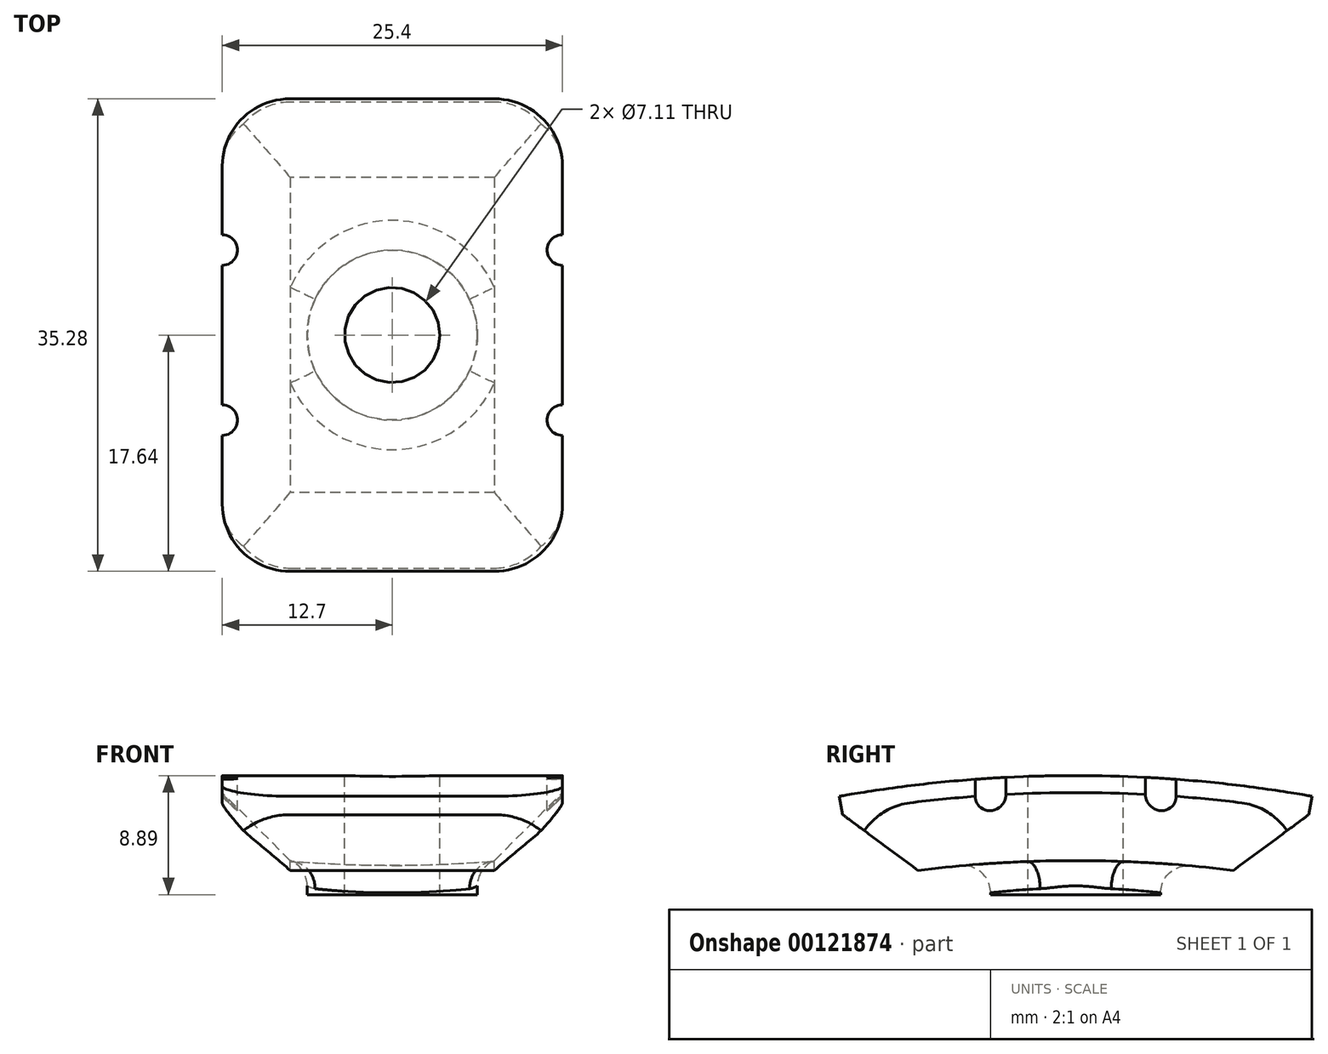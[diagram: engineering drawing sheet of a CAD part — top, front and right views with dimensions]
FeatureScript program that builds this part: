
annotation { "Feature Type Name" : "Feature", "Feature Type Description" : "" }
export const myFeature = defineFeature(function(context is Context, id is Id, definition is map)
    precondition{}
    {
        {
            var Q0;
            Q0=qCreatedBy(makeId("Right.planeOp"),FACE);
            var sketch = newSketch(context, id + "F0", { "sketchPlane" : qUnion([Q0])});
            skArc(sketch, "E0", {"start": v(17.64, -1.54) * mm, "mid": v(0, 0) * mm, "end": v(-17.64, -1.54) * mm});
            skArc(sketch, "E1", {"start": v(16.54, -7.8) * mm, "mid": v(0, -6.35) * mm, "end": v(-16.54, -7.8) * mm});
            skLineSegment(sketch, "E2", {"start": v(-16.54, -7.8) * mm, "end": v(-17.64, -1.54) * mm});
            skLineSegment(sketch, "E3.MirrorCS", {"start": v(16.54, -7.8) * mm, "end": v(17.64, -1.54) * mm});
            skSolve(sketch);
        }
        {
            var Q0;
            Q0=makeQuery(id+"F0.imprint","IMPRINT",FACE,{"disambiguationData":[TD([[makeQuery(id+"F0.imprint","IMPRINT",EDGE,{"derivedFrom":sQuery(id+"F0.wireOp",EDGE,"E0")}),1.0]])]});
            extrude(context, id + "F1", {"entities" : qUnion([Q0]), "endBound" : BoundingType.SYMMETRIC, "depth" : 25.4 * mm});
        }
        {
            var Q0;
            Q0=qCreatedBy(makeId("Top.planeOp"),FACE);
            var sketch = newSketch(context, id + "F2", { "sketchPlane" : qUnion([Q0])});
            skCircle(sketch, "E4", {"center": v(0, 0) * mm, "radius": 3.56 * mm});
            skLineSegment(sketch, "E5.bottom", {"start": v(12.7, 6.35) * mm, "end": v(-12.7, 6.35) * mm});
            skLineSegment(sketch, "E5.top", {"start": v(12.7, -6.35) * mm, "end": v(-12.7, -6.35) * mm});
            skLineSegment(sketch, "E5.left", {"start": v(12.7, 6.35) * mm, "end": v(12.7, -6.35) * mm});
            skLineSegment(sketch, "E5.right", {"start": v(-12.7, 6.35) * mm, "end": v(-12.7, -6.35) * mm});
            skCircle(sketch, "E6", {"center": v(12.7, 6.35) * mm, "radius": 1.14 * mm});
            skCircle(sketch, "E7", {"center": v(-12.7, 6.35) * mm, "radius": 1.14 * mm});
            skCircle(sketch, "E8", {"center": v(12.7, -6.35) * mm, "radius": 1.14 * mm});
            skCircle(sketch, "E9", {"center": v(-12.7, -6.35) * mm, "radius": 1.14 * mm});
            skSolve(sketch);
        }
        {
            var Q0;
            Q0=makeQuery(id+"F2.imprint","IMPRINT",FACE,{"disambiguationData":[TD([[makeQuery(id+"F2.imprint","IMPRINT",EDGE,{"derivedFrom":sQuery(id+"F2.wireOp",EDGE,"E4")}),1.0]])]});
            extrude(context, id + "F3", {"entities" : qUnion([Q0]), "operationType" : NewBodyOperationType.REMOVE, "oppositeDirection" : true, "depth" : 25.4 * mm});
        }
        {
            var Q0;
            {var subQ0=sQuery(id+"F2.wireOp",EDGE,"E5.right");var subQ1=sQuery(id+"F2.wireOp",EDGE,"E5.bottom");var subQ2=makeQuery(id+"F2.imprint","INTERSECT",VERTEX,{"derivedFrom":[subQ1,subQ0]});Q0=makeQuery(id+"F2.imprint","IMPRINT",FACE,{"disambiguationData":[TD([[makeQuery(id+"F2.imprint","IMPRINT",EDGE,{"disambiguationData":[TD([[subQ2,1.0]])],"derivedFrom":subQ1}),-1.0]])]});}
            var Q1;
            {var subQ0=sQuery(id+"F2.wireOp",EDGE,"E5.right");var subQ1=sQuery(id+"F2.wireOp",EDGE,"E5.bottom");var subQ2=makeQuery(id+"F2.imprint","INTERSECT",VERTEX,{"derivedFrom":[subQ1,subQ0]});Q1=makeQuery(id+"F2.imprint","IMPRINT",FACE,{"disambiguationData":[TD([[makeQuery(id+"F2.imprint","IMPRINT",EDGE,{"disambiguationData":[TD([[subQ2,1.0]])],"derivedFrom":subQ1}),1.0]])]});}
            var Q2;
            {var subQ0=sQuery(id+"F2.wireOp",EDGE,"E5.left");var subQ1=sQuery(id+"F2.wireOp",EDGE,"E5.bottom");var subQ2=makeQuery(id+"F2.imprint","INTERSECT",VERTEX,{"derivedFrom":[subQ1,subQ0]});Q2=makeQuery(id+"F2.imprint","IMPRINT",FACE,{"disambiguationData":[TD([[makeQuery(id+"F2.imprint","IMPRINT",EDGE,{"disambiguationData":[TD([[subQ2,-1.0]])],"derivedFrom":subQ1}),-1.0]])]});}
            var Q3;
            {var subQ0=sQuery(id+"F2.wireOp",EDGE,"E5.left");var subQ1=sQuery(id+"F2.wireOp",EDGE,"E5.bottom");var subQ2=makeQuery(id+"F2.imprint","INTERSECT",VERTEX,{"derivedFrom":[subQ1,subQ0]});Q3=makeQuery(id+"F2.imprint","IMPRINT",FACE,{"disambiguationData":[TD([[makeQuery(id+"F2.imprint","IMPRINT",EDGE,{"disambiguationData":[TD([[subQ2,-1.0]])],"derivedFrom":subQ1}),1.0]])]});}
            var Q4;
            {var subQ0=sQuery(id+"F2.wireOp",EDGE,"E5.right");var subQ1=sQuery(id+"F2.wireOp",EDGE,"E5.top");var subQ2=makeQuery(id+"F2.imprint","INTERSECT",VERTEX,{"derivedFrom":[subQ1,subQ0]});Q4=makeQuery(id+"F2.imprint","IMPRINT",FACE,{"disambiguationData":[TD([[makeQuery(id+"F2.imprint","IMPRINT",EDGE,{"disambiguationData":[TD([[subQ2,1.0]])],"derivedFrom":subQ1}),1.0]])]});}
            var Q5;
            {var subQ0=sQuery(id+"F2.wireOp",EDGE,"E5.right");var subQ1=sQuery(id+"F2.wireOp",EDGE,"E5.top");var subQ2=makeQuery(id+"F2.imprint","INTERSECT",VERTEX,{"derivedFrom":[subQ1,subQ0]});Q5=makeQuery(id+"F2.imprint","IMPRINT",FACE,{"disambiguationData":[TD([[makeQuery(id+"F2.imprint","IMPRINT",EDGE,{"disambiguationData":[TD([[subQ2,1.0]])],"derivedFrom":subQ1}),-1.0]])]});}
            var Q6;
            {var subQ0=sQuery(id+"F2.wireOp",EDGE,"E5.left");var subQ1=sQuery(id+"F2.wireOp",EDGE,"E5.top");var subQ2=makeQuery(id+"F2.imprint","INTERSECT",VERTEX,{"derivedFrom":[subQ1,subQ0]});Q6=makeQuery(id+"F2.imprint","IMPRINT",FACE,{"disambiguationData":[TD([[makeQuery(id+"F2.imprint","IMPRINT",EDGE,{"disambiguationData":[TD([[subQ2,-1.0]])],"derivedFrom":subQ1}),1.0]])]});}
            var Q7;
            {var subQ0=sQuery(id+"F2.wireOp",EDGE,"E5.left");var subQ1=sQuery(id+"F2.wireOp",EDGE,"E5.top");var subQ2=makeQuery(id+"F2.imprint","INTERSECT",VERTEX,{"derivedFrom":[subQ1,subQ0]});Q7=makeQuery(id+"F2.imprint","IMPRINT",FACE,{"disambiguationData":[TD([[makeQuery(id+"F2.imprint","IMPRINT",EDGE,{"disambiguationData":[TD([[subQ2,-1.0]])],"derivedFrom":subQ1}),-1.0]])]});}
            extrude(context, id + "F4", {"entities" : qUnion([Q0, Q1, Q2, Q3, Q4, Q5, Q6, Q7]), "operationType" : NewBodyOperationType.REMOVE, "oppositeDirection" : true, "depth" : 25.4 * mm});
        }
        {
            var Q0;
            Q0=makeQuery(id+"F1.opExtrude","CAP_EDGE",EDGE,{"disambiguationData":[OSD([sQuery(id+"F0.wireOp",EDGE,"E1")])],"isStart":true});
            var Q1;
            Q1=makeQuery(id+"F1.opExtrude","SWEPT_EDGE",EDGE,{"disambiguationData":[OSD([sQuery(id+"F0.wireOp",EDGE,"E1"),sQuery(id+"F0.wireOp",EDGE,"E2")])]});
            var Q2;
            Q2=makeQuery(id+"F1.opExtrude","CAP_EDGE",EDGE,{"disambiguationData":[OSD([sQuery(id+"F0.wireOp",EDGE,"E1")])],"isStart":false});
            var Q3;
            Q3=makeQuery(id+"F1.opExtrude","SWEPT_EDGE",EDGE,{"disambiguationData":[OSD([sQuery(id+"F0.wireOp",EDGE,"E1"),sQuery(id+"F0.wireOp",EDGE,"E3.MirrorCS")])]});
            chamfer(context, id + "F5", {"entities" : qUnion([Q0, Q1, Q2, Q3]), "width" : 5.08 * mm, "tangentPropagation" : true});
        }
        {
            var Q0;
            Q0=makeQuery(id+"F2.imprint","IMPRINT",FACE,{"disambiguationData":[TD([[makeQuery(id+"F2.imprint","IMPRINT",EDGE,{"derivedFrom":sQuery(id+"F2.wireOp",EDGE,"E4")}),-1.0]])]});
            cPlane(context, id + "F6", {"entities" : qUnion([Q0]), "cplaneType" : CPlaneType.OFFSET, "offset" : 6.35 * mm, "oppositeDirection" : true, "width" : 152.4 * mm, "height" : 152.4 * mm});
        }
        {
            var Q0;
            Q0=qCreatedBy(id+"F6.planeOp",FACE);
            var sketch = newSketch(context, id + "F7", { "sketchPlane" : qUnion([Q0])});
            skCircle(sketch, "E10", {"center": v(0, 0) * mm, "radius": 3.56 * mm});
            skCircle(sketch, "E11", {"center": v(0, 0) * mm, "radius": 6.35 * mm});
            skSolve(sketch);
        }
        {
            var Q0;
            Q0=makeQuery(id+"F7.imprint","IMPRINT",FACE,{"disambiguationData":[TD([[makeQuery(id+"F7.imprint","IMPRINT",EDGE,{"derivedFrom":sQuery(id+"F7.wireOp",EDGE,"E10")}),-1.0]])]});
            extrude(context, id + "F8", {"entities" : qUnion([Q0]), "oppositeDirection" : true, "depth" : 2.54 * mm});
        }
        {
            var Q0;
            Q0=makeQuery(id+"F1.opExtrude","SWEPT_BODY",BODY,{"disambiguationData":[OSD([sQuery(id+"F0.wireOp",EDGE,"E0"),sQuery(id+"F0.wireOp",EDGE,"E1"),sQuery(id+"F0.wireOp",EDGE,"E2"),sQuery(id+"F0.wireOp",EDGE,"E3.MirrorCS")])]});
            var Q1;
            Q1=makeQuery(id+"F8.opExtrude","SWEPT_BODY",BODY,{"disambiguationData":[OSD([sQuery(id+"F7.wireOp",EDGE,"E10"),sQuery(id+"F7.wireOp",EDGE,"E11")])]});
            booleanBodies(context, id + "F9", {"operationType" : BooleanOperationType.UNION, "tools" : qUnion([Q0, Q1])});
        }
        {
            var Q0;
            Q0=makeQuery(id+"F9.opBoolean","INTERSECT",EDGE,{"derivedFrom":[makeQuery(id+"F1.opExtrude","SWEPT_FACE",FACE,{"disambiguationData":[OSD([sQuery(id+"F0.wireOp",EDGE,"E1")])]}),makeQuery(id+"F8.opExtrude","SWEPT_FACE",FACE,{"disambiguationData":[OSD([sQuery(id+"F7.wireOp",EDGE,"E11")])]})]});
            fillet(context, id + "F10", {"entities" : qUnion([Q0]), "radius" : 2.03 * mm, "tangentPropagation" : true, "allowEdgeOverflow" : false});
        }
        {
            var Q0;
            Q0=makeQuery(id+"F1.opExtrude","CAP_EDGE",EDGE,{"disambiguationData":[OSD([sQuery(id+"F0.wireOp",EDGE,"E3.MirrorCS")])],"isStart":false});
            var Q1;
            Q1=makeQuery(id+"F1.opExtrude","CAP_EDGE",EDGE,{"disambiguationData":[OSD([sQuery(id+"F0.wireOp",EDGE,"E3.MirrorCS")])],"isStart":true});
            var Q2;
            Q2=makeQuery(id+"F1.opExtrude","CAP_EDGE",EDGE,{"disambiguationData":[OSD([sQuery(id+"F0.wireOp",EDGE,"E2")])],"isStart":false});
            var Q3;
            Q3=makeQuery(id+"F1.opExtrude","CAP_EDGE",EDGE,{"disambiguationData":[OSD([sQuery(id+"F0.wireOp",EDGE,"E2")])],"isStart":true});
            fillet(context, id + "F11", {"entities" : qUnion([Q0, Q1, Q2, Q3]), "radius" : 5.08 * mm, "tangentPropagation" : true, "allowEdgeOverflow" : false});
        }
    });
